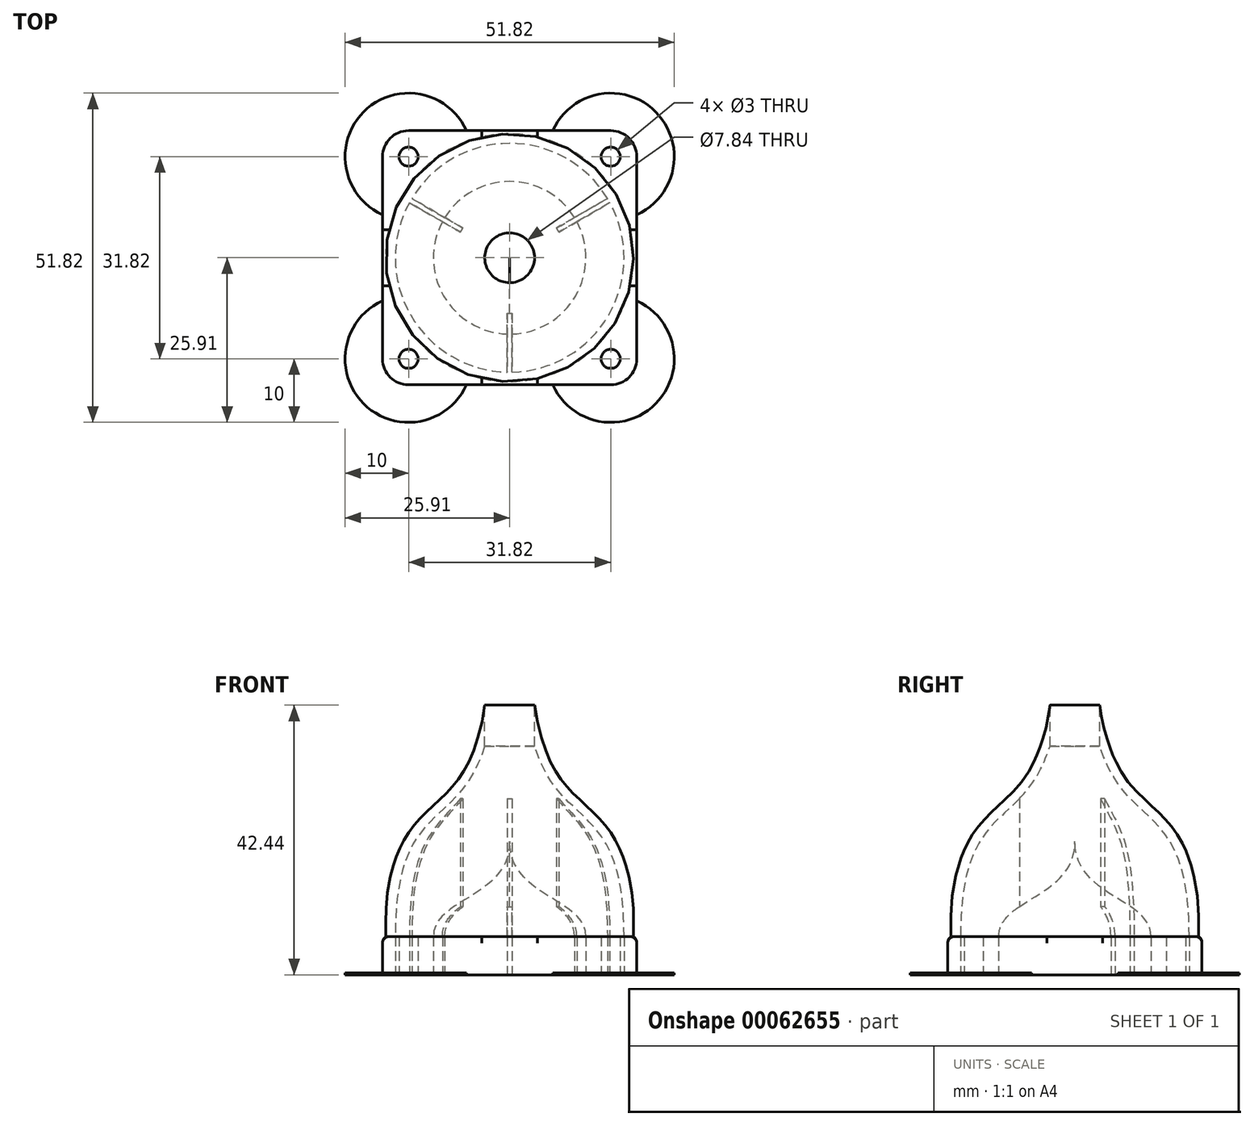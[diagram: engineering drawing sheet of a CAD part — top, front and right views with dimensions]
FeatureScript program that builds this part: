
annotation { "Feature Type Name" : "Feature", "Feature Type Description" : "" }
export const myFeature = defineFeature(function(context is Context, id is Id, definition is map)
    precondition{}
    {
        {
            var Q0;
            Q0=qCreatedBy(makeId("Top.planeOp"),FACE);
            var sketch = newSketch(context, id + "F0", { "sketchPlane" : qUnion([Q0])});
            skLineSegment(sketch, "E0.bottom", {"start": v(-15.9, 20) * mm, "end": v(15.9, 20) * mm});
            skLineSegment(sketch, "E0.top", {"start": v(-15.9, -20) * mm, "end": v(15.9, -20) * mm});
            skLineSegment(sketch, "E0.left", {"start": v(-20, 15.9) * mm, "end": v(-20, -15.9) * mm});
            skLineSegment(sketch, "E0.right", {"start": v(20, 15.9) * mm, "end": v(20, -15.9) * mm});
            skCircle(sketch, "E1", {"center": v(-15.9, 15.9) * mm, "radius": 1.5 * mm});
            skCircle(sketch, "E2.1.0", {"center": v(-15.9, -15.9) * mm, "radius": 1.5 * mm});
            skCircle(sketch, "E2.2.0", {"center": v(15.9, -15.9) * mm, "radius": 1.5 * mm});
            skCircle(sketch, "E2.3.0", {"center": v(15.9, 15.9) * mm, "radius": 1.5 * mm});
            skPoint(sketch, "E2.center", {"position": v(0, 0) * mm});
            skLineSegment(sketch, "E3", {"start": v(-20, 20) * mm, "end": v(20, -20) * mm, "construction": true});
            skArc(sketch, "E4", {"start": v(-15.9, 20) * mm, "mid": v(-18.8, 18.8) * mm, "end": v(-20, 15.9) * mm});
            skArc(sketch, "E5", {"start": v(-20, -15.9) * mm, "mid": v(-18.8, -18.8) * mm, "end": v(-15.9, -20) * mm});
            skCircle(sketch, "E6", {"center": v(0, 0) * mm, "radius": 18 * mm});
            skCircle(sketch, "E7", {"center": v(0, 0) * mm, "radius": 12 * mm});
            skPoint(sketch, "E8.visualSharp", {"position": v(20, 20) * mm});
            skArc(sketch, "E8.filletArc", {"start": v(20, 15.9) * mm, "mid": v(18.8, 18.8) * mm, "end": v(15.9, 20) * mm});
            skPoint(sketch, "E9.visualSharp", {"position": v(20, -20) * mm});
            skArc(sketch, "E9.filletArc", {"start": v(15.9, -20) * mm, "mid": v(18.8, -18.8) * mm, "end": v(20, -15.9) * mm});
            skSolve(sketch);
        }
        {
            var Q0;
            {var subQ0=sQuery(id+"F0.wireOp",EDGE,"E0.bottom");Q0=makeQuery(id+"F0.imprint","IMPRINT",FACE,{"disambiguationData":[TD([[makeQuery(id+"F0.imprint","IMPRINT",EDGE,{"derivedFrom":subQ0}),-1.0]])]});}
            var Q1;
            Q1=makeQuery(id+"F0.imprint","IMPRINT",FACE,{"disambiguationData":[TD([[makeQuery(id+"F0.imprint","IMPRINT",EDGE,{"derivedFrom":sQuery(id+"F0.wireOp",EDGE,"E7")}),1.0]])]});
            var Q2;
            {var subQ1=sQuery(id+"F0.wireOp",EDGE,"E0.right");Q2=makeQuery(id+"F0.imprint","IMPRINT",FACE,{"disambiguationData":[TD([[makeQuery(id+"F0.imprint","IMPRINT",EDGE,{"derivedFrom":subQ1}),1.0]])]});}
            extrude(context, id + "F1", {"entities" : qUnion([Q0, Q1, Q2]), "depth" : 6 * mm});
        }
        {
            var Q0;
            Q0=qCreatedBy(makeId("Right.planeOp"),FACE);
            var sketch = newSketch(context, id + "F2", { "sketchPlane" : qUnion([Q0])});
            skLineSegment(sketch, "E10.0", {"start": v(-18, 6) * mm, "end": v(18, 6) * mm, "construction": true});
            skFitSpline(sketch, "E11.MirrorCS", {"points": [v(-18, 6) * mm, v(-2.05, 47.13) * mm], "startDerivative": vector(0, 78.33) * mm, "endDerivative": vector(5.6, 84.46) * mm});
            skFitSpline(sketch, "E12.0", {"points": [v(-19.5, 6) * mm, v(-19.5, 9.33) * mm, v(-19.16, 13.44) * mm, v(-18.16, 17.6) * mm, v(-17.16, 20.2) * mm, v(-15.95, 22.33) * mm, v(-14.6, 24.09) * mm, v(-13.17, 25.57) * mm, v(-11.74, 26.9) * mm, v(-10.36, 28.2) * mm, v(-9.04, 29.57) * mm, v(-7.8, 31.16) * mm, v(-6.66, 33.1) * mm, v(-5.6, 35.51) * mm, v(-4.4, 39.58) * mm, v(-3.78, 43.77) * mm, v(-3.55, 47.23) * mm]});
            skLineSegment(sketch, "E13", {"start": v(-19.5, 6) * mm, "end": v(-18, 6) * mm});
            skLineSegment(sketch, "E14", {"start": v(-5.5, 36) * mm, "end": v(-5.5, 56) * mm});
            skLineSegment(sketch, "E15", {"start": v(-5.5, 56) * mm, "end": v(-3.92, 56) * mm});
            skLineSegment(sketch, "E16", {"start": v(-3.92, 36) * mm, "end": v(-3.92, 56) * mm});
            skLineSegment(sketch, "E17.0", {"start": v(-12, 6) * mm, "end": v(12, 6) * mm, "construction": true});
            skFitSpline(sketch, "E18", {"points": [v(-12, 6) * mm, v(0, 21) * mm], "startDerivative": vector(0, 18.35) * mm, "endDerivative": vector(0, 26.65) * mm});
            skLineSegment(sketch, "E19", {"start": v(0, 21) * mm, "end": v(0, 6) * mm});
            skLineSegment(sketch, "E20", {"start": v(0, 6) * mm, "end": v(-12, 6) * mm});
            skSolve(sketch);
        }
        {
            var Q0;
            Q0=makeQuery(id+"F2.imprint","IMPRINT",FACE,{"disambiguationData":[TD([[makeQuery(id+"F2.imprint","IMPRINT",EDGE,{"derivedFrom":sQuery(id+"F2.wireOp",EDGE,"E11.MirrorCS")}),1.0]])]});
            var Q1;
            Q1=makeQuery(id+"F2.imprint","IMPRINT",FACE,{"disambiguationData":[TD([[makeQuery(id+"F2.imprint","IMPRINT",EDGE,{"derivedFrom":sQuery(id+"F2.wireOp",EDGE,"E18")}),-1.0]])]});
            var Q2;
            Q2=sQuery(id+"F2.wireOp",EDGE,"E19");
            revolve(context, id + "F3", {"entities" : qUnion([Q0, Q1]), "axis" : qUnion([Q2]), "revolveType" : RevolveType.FULL});
        }
        {
            var Q0;
            Q0=qCreatedBy(makeId("Top.planeOp"),FACE);
            var sketch = newSketch(context, id + "F4", { "sketchPlane" : qUnion([Q0])});
            skArc(sketch, "E21.0", {"start": v(-0.37, -18) * mm, "mid": v(0, -18) * mm, "end": v(0.37, -18) * mm});
            skLineSegment(sketch, "E22", {"start": v(-0.38, -18) * mm, "end": v(-0.38, -8.74) * mm});
            skArc(sketch, "E23", {"start": v(-0.38, -8.74) * mm, "mid": v(0, -8.75) * mm, "end": v(0.37, -8.74) * mm});
            skLineSegment(sketch, "E24.MirrorCS", {"start": v(0.38, -18) * mm, "end": v(0.38, -8.74) * mm});
            skLineSegment(sketch, "E25.1.0", {"start": v(15.77, 8.67) * mm, "end": v(7.76, 4.05) * mm});
            skArc(sketch, "E25.1.1", {"start": v(15.77, 8.67) * mm, "mid": v(15.59, 9) * mm, "end": v(15.4, 9.32) * mm});
            skLineSegment(sketch, "E25.1.2", {"start": v(15.4, 9.32) * mm, "end": v(7.38, 4.7) * mm});
            skArc(sketch, "E25.1.3", {"start": v(7.76, 4.05) * mm, "mid": v(7.58, 4.38) * mm, "end": v(7.38, 4.7) * mm});
            skLineSegment(sketch, "E25.2.0", {"start": v(-15.4, 9.32) * mm, "end": v(-7.38, 4.7) * mm});
            skArc(sketch, "E25.2.1", {"start": v(-15.4, 9.32) * mm, "mid": v(-15.59, 9) * mm, "end": v(-15.77, 8.67) * mm});
            skLineSegment(sketch, "E25.2.2", {"start": v(-15.77, 8.67) * mm, "end": v(-7.76, 4.05) * mm});
            skArc(sketch, "E25.2.3", {"start": v(-7.38, 4.7) * mm, "mid": v(-7.58, 4.38) * mm, "end": v(-7.76, 4.05) * mm});
            skSolve(sketch);
        }
        {
            var Q0;
            Q0=qSketchRegion(id+"F4",true);
            var Q1;
            Q1=makeQuery(id+"F3.opRevolve","SWEPT_FACE",FACE,{"disambiguationData":[OSD([sQuery(id+"F2.wireOp",EDGE,"E11.MirrorCS")])]});
            extrude(context, id + "F5", {"entities" : qUnion([Q0]), "operationType" : NewBodyOperationType.ADD, "endBound" : BoundingType.UP_TO_SURFACE, "endBoundEntityFace" : qUnion([Q1]), "depth" : 25 * mm});
        }
        {
            var Q0;
            Q0=makeQuery(id+"F1.opExtrude","CAP_EDGE",EDGE,{"disambiguationData":[OSD([sQuery(id+"F0.wireOp",EDGE,"E0.left")])],"isStart":false});
            fillet(context, id + "F6", {"entities" : qUnion([Q0]), "radius" : 1 * mm, "tangentPropagation" : true, "allowEdgeOverflow" : false});
        }
        {
            var Q0;
            Q0=makeQuery(id+"F5.boolean.opBoolean","MERGE",FACE,{"derivedFrom":[makeQuery(id+"F1.opExtrude","CAP_FACE",FACE,{"disambiguationData":[OSD([sQuery(id+"F0.wireOp",EDGE,"E0.bottom"),sQuery(id+"F0.wireOp",EDGE,"E0.top"),sQuery(id+"F0.wireOp",EDGE,"E0.left"),sQuery(id+"F0.wireOp",EDGE,"E0.right"),sQuery(id+"F0.wireOp",EDGE,"E1"),sQuery(id+"F0.wireOp",EDGE,"E2.1.0"),sQuery(id+"F0.wireOp",EDGE,"E2.2.0"),sQuery(id+"F0.wireOp",EDGE,"E2.3.0"),sQuery(id+"F0.wireOp",EDGE,"E4"),sQuery(id+"F0.wireOp",EDGE,"E5"),sQuery(id+"F0.wireOp",EDGE,"E6"),sQuery(id+"F0.wireOp",EDGE,"E8.filletArc"),sQuery(id+"F0.wireOp",EDGE,"E9.filletArc")])],"isStart":true}),makeQuery(id+"F1.opExtrude","CAP_FACE",FACE,{"disambiguationData":[OSD([sQuery(id+"F0.wireOp",EDGE,"E7")])],"isStart":true}),makeQuery(id+"F5.opExtrude","CAP_FACE",FACE,{"disambiguationData":[OSD([sQuery(id+"F4.wireOp",EDGE,"E21.0"),sQuery(id+"F4.wireOp",EDGE,"E22"),sQuery(id+"F4.wireOp",EDGE,"E23"),sQuery(id+"F4.wireOp",EDGE,"E24.MirrorCS")])],"isStart":true}),makeQuery(id+"F5.opExtrude","CAP_FACE",FACE,{"disambiguationData":[OSD([sQuery(id+"F4.wireOp",EDGE,"E25.1.0"),sQuery(id+"F4.wireOp",EDGE,"E25.1.1"),sQuery(id+"F4.wireOp",EDGE,"E25.1.2"),sQuery(id+"F4.wireOp",EDGE,"E25.1.3")])],"isStart":true}),makeQuery(id+"F5.opExtrude","CAP_FACE",FACE,{"disambiguationData":[OSD([sQuery(id+"F4.wireOp",EDGE,"E25.2.0"),sQuery(id+"F4.wireOp",EDGE,"E25.2.1"),sQuery(id+"F4.wireOp",EDGE,"E25.2.2"),sQuery(id+"F4.wireOp",EDGE,"E25.2.3")])],"isStart":true})]});
            var sketch = newSketch(context, id + "F7", { "sketchPlane" : qUnion([Q0])});
            skArc(sketch, "E26", {"start": v(-6.78, 20) * mm, "mid": v(-22.98, 22.98) * mm, "end": v(-20, 6.78) * mm});
            skArc(sketch, "E27", {"start": v(-20, -6.78) * mm, "mid": v(-22.98, -22.98) * mm, "end": v(-6.78, -20) * mm});
            skArc(sketch, "E28", {"start": v(6.78, -20) * mm, "mid": v(22.98, -22.98) * mm, "end": v(20, -6.78) * mm});
            skArc(sketch, "E29", {"start": v(20, 6.78) * mm, "mid": v(22.98, 22.98) * mm, "end": v(6.78, 20) * mm});
            skLineSegment(sketch, "E30.0", {"start": v(-20, -6.78) * mm, "end": v(-20, 6.78) * mm});
            skLineSegment(sketch, "E31.0", {"start": v(-6.78, 20) * mm, "end": v(6.78, 20) * mm});
            skLineSegment(sketch, "E32.0", {"start": v(20, -6.78) * mm, "end": v(20, 6.78) * mm});
            skLineSegment(sketch, "E33.0", {"start": v(-6.78, -20) * mm, "end": v(6.78, -20) * mm});
            skPoint(sketch, "E34.orphan", {"position": v(-20, 15.9) * mm});
            skPoint(sketch, "E35.orphan", {"position": v(-15.9, 20) * mm});
            skPoint(sketch, "E36.orphan", {"position": v(15.9, 20) * mm});
            skPoint(sketch, "E37.orphan", {"position": v(20, 15.9) * mm});
            skPoint(sketch, "E38.orphan", {"position": v(20, -15.9) * mm});
            skPoint(sketch, "E39.orphan", {"position": v(15.9, -20) * mm});
            skPoint(sketch, "E40.orphan", {"position": v(-15.9, -20) * mm});
            skPoint(sketch, "E41.orphan", {"position": v(-20, -15.9) * mm});
            skSolve(sketch);
        }
        {
            var Q0;
            {var subQ0=sQuery(id+"F7.wireOp",EDGE,"E28");Q0=makeQuery(id+"F7.imprint","IMPRINT",FACE,{"disambiguationData":[TD([[makeQuery(id+"F7.imprint","IMPRINT",EDGE,{"derivedFrom":subQ0}),1.0]])]});}
            var Q1;
            {var subQ0=sQuery(id+"F7.wireOp",EDGE,"E27");Q1=makeQuery(id+"F7.imprint","IMPRINT",FACE,{"disambiguationData":[TD([[makeQuery(id+"F7.imprint","IMPRINT",EDGE,{"derivedFrom":subQ0}),1.0]])]});}
            var Q2;
            {var subQ0=sQuery(id+"F7.wireOp",EDGE,"E26");Q2=makeQuery(id+"F7.imprint","IMPRINT",FACE,{"disambiguationData":[TD([[makeQuery(id+"F7.imprint","IMPRINT",EDGE,{"derivedFrom":subQ0}),1.0]])]});}
            var Q3;
            {var subQ0=sQuery(id+"F7.wireOp",EDGE,"E29");Q3=makeQuery(id+"F7.imprint","IMPRINT",FACE,{"disambiguationData":[TD([[makeQuery(id+"F7.imprint","IMPRINT",EDGE,{"derivedFrom":subQ0}),1.0]])]});}
            extrude(context, id + "F8", {"entities" : qUnion([Q0, Q1, Q2, Q3]), "operationType" : NewBodyOperationType.ADD, "oppositeDirection" : true, "depth" : 0.3 * mm});
        }
    });
